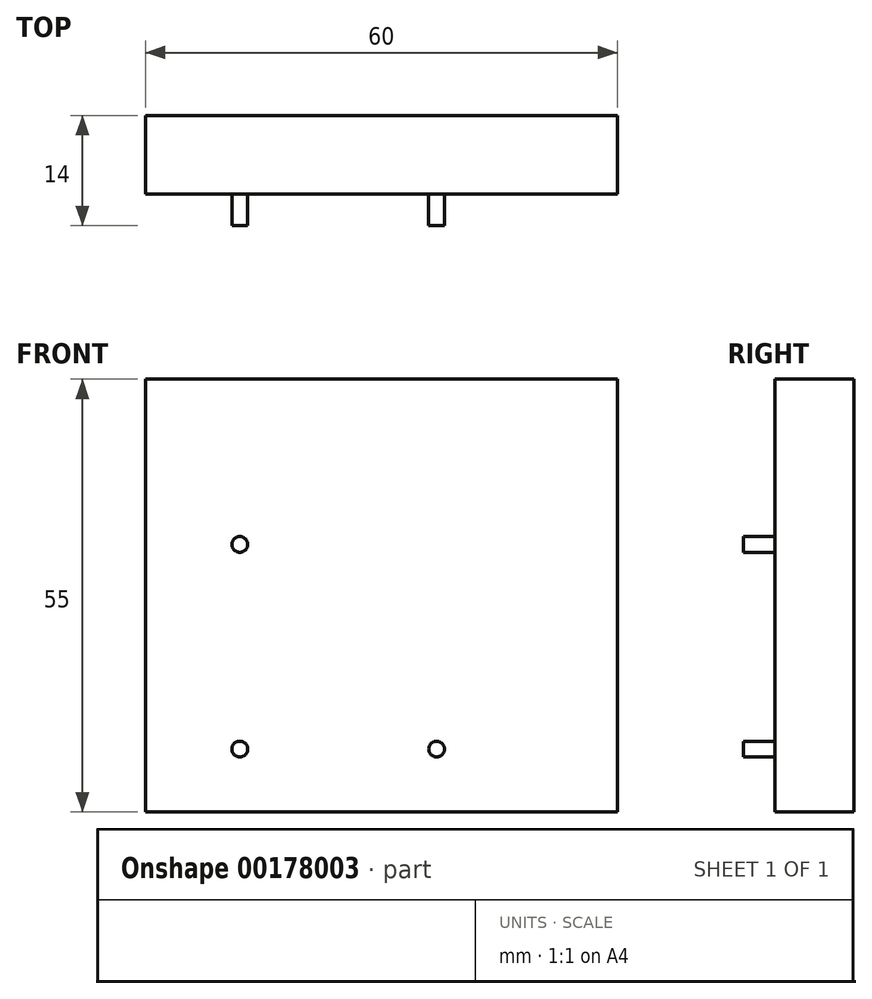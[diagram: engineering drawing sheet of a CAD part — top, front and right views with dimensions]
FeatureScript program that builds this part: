
annotation { "Feature Type Name" : "Feature", "Feature Type Description" : "" }
export const myFeature = defineFeature(function(context is Context, id is Id, definition is map)
    precondition{}
    {
        {
            var Q0;
            Q0=qCreatedBy(makeId("Right.planeOp"),FACE);
            var sketch = newSketch(context, id + "F0", { "sketchPlane" : qUnion([Q0])});
            skLineSegment(sketch, "E0.bottom", {"start": v(5, 20) * mm, "end": v(-5, 20) * mm});
            skLineSegment(sketch, "E0.top", {"start": v(5, -20) * mm, "end": v(-5, -20) * mm});
            skLineSegment(sketch, "E0.left", {"start": v(5, 20) * mm, "end": v(5, -20) * mm});
            skLineSegment(sketch, "E0.right", {"start": v(-5, 20) * mm, "end": v(-5, -20) * mm});
            skPoint(sketch, "E0.middle", {"position": v(0, 0) * mm});
            skSolve(sketch);
        }
        {
            var Q0;
            Q0 = qSketchRegion(id + "F0", true);
            extrude(context, id + "F1", {"entities" : qUnion([Q0]), "depth" : 30 * mm, "hasSecondDirection" : true, "secondDirectionOppositeDirection" : true, "secondDirectionDepth" : 30 * mm});
        }
        {
            var Q0;
            Q0=makeQuery(id+"F1.opExtrude","SWEPT_FACE",FACE,{"disambiguationData":[OSD([sQuery(id+"F0.wireOp",EDGE,"E0.right")])]});
            var sketch = newSketch(context, id + "F2", { "sketchPlane" : qUnion([Q0])});
            skCircle(sketch, "E1", {"center": v(-18, 14) * mm, "radius": 1 * mm});
            skCircle(sketch, "E2", {"center": v(-18, -12) * mm, "radius": 1 * mm});
            skCircle(sketch, "E3", {"center": v(7, -12) * mm, "radius": 1 * mm});
            skSolve(sketch);
        }
        {
            var Q0;
            Q0 = qSketchRegion(id + "F2", true);
            extrude(context, id + "F3", {"entities" : qUnion([Q0]), "operationType" : NewBodyOperationType.ADD, "depth" : 4 * mm});
        }
        {
            var Q0;
            Q0=makeQuery(id+"F1.opExtrude","SWEPT_FACE",FACE,{"disambiguationData":[OSD([sQuery(id+"F0.wireOp",EDGE,"E0.bottom")])]});
            extrude(context, id + "F4", {"entities" : qUnion([Q0]), "operationType" : NewBodyOperationType.ADD, "depth" : 15 * mm});
        }
    });
